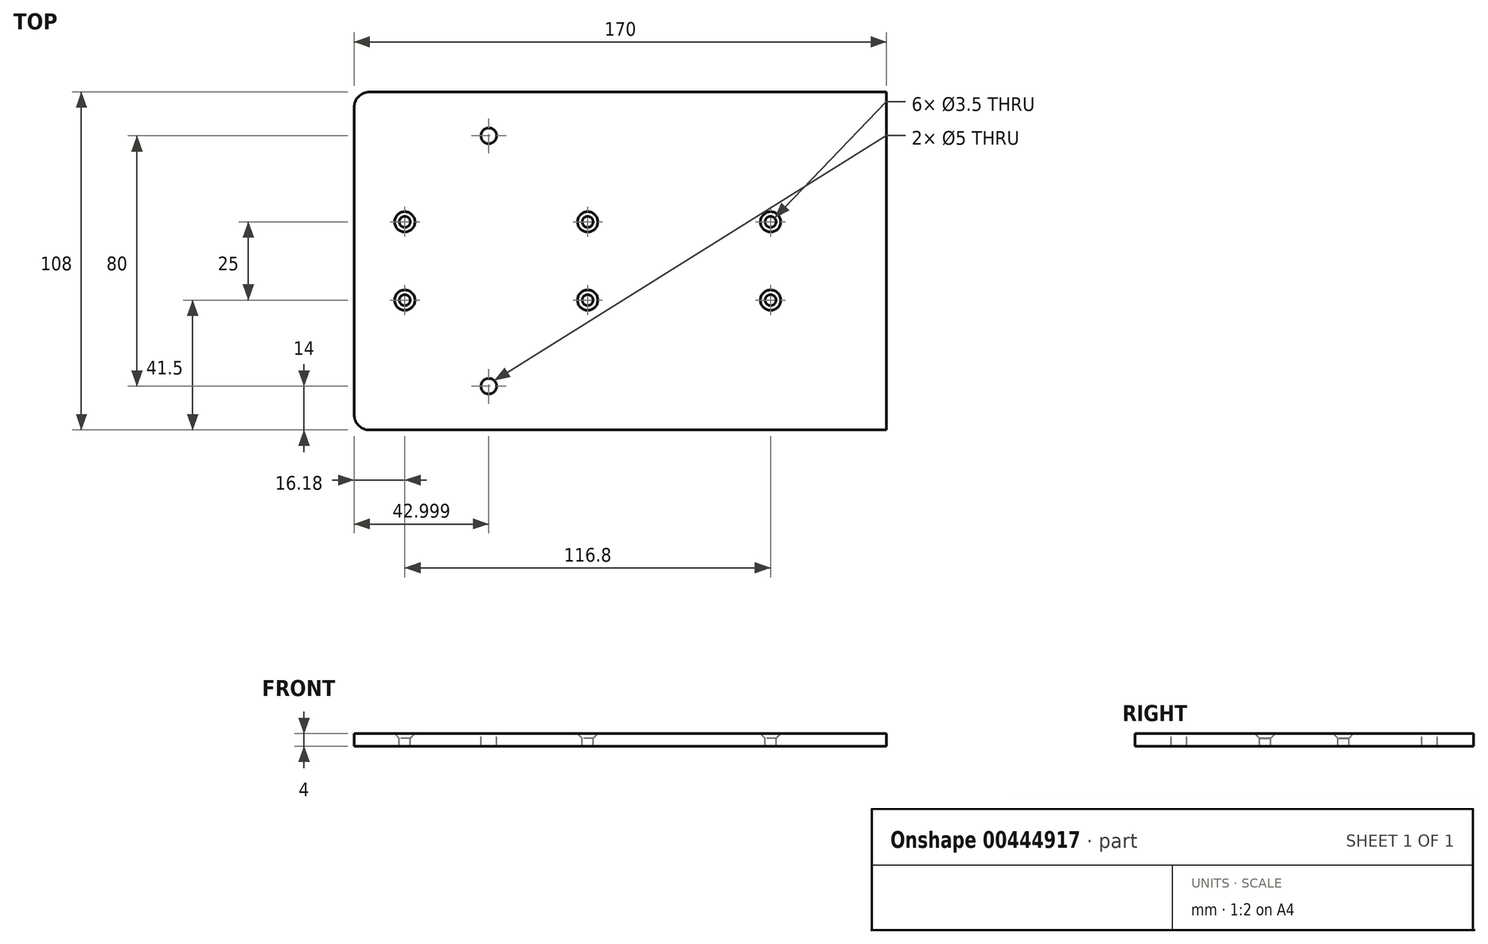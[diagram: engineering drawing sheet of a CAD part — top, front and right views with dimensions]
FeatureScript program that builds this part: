
annotation { "Feature Type Name" : "Feature", "Feature Type Description" : "" }
export const myFeature = defineFeature(function(context is Context, id is Id, definition is map)
    precondition{}
    {
        {
            var Q0;
            Q0=qCreatedBy(makeId("Top.planeOp"),FACE);
            var sketch = newSketch(context, id + "F0", { "sketchPlane" : qUnion([Q0])});
            skLineSegment(sketch, "E0.bottom", {"start": v(-74.58, 0) * mm, "end": v(95.42, 0) * mm});
            skLineSegment(sketch, "E0.top", {"start": v(-74.58, 54) * mm, "end": v(95.42, 54) * mm});
            skLineSegment(sketch, "E0.left", {"start": v(-74.58, 0) * mm, "end": v(-74.58, 54) * mm});
            skLineSegment(sketch, "E0.right", {"start": v(95.42, 0) * mm, "end": v(95.42, 54) * mm});
            skSolve(sketch);
        }
        {
            var Q0;
            Q0=makeQuery(id+"F0.imprint","IMPRINT",FACE,{"disambiguationData":[TD([[makeQuery(id+"F0.imprint","IMPRINT",EDGE,{"derivedFrom":sQuery(id+"F0.wireOp",EDGE,"E0.bottom")}),1.0]])]});
            extrude(context, id + "F1", {"entities" : qUnion([Q0]), "depth" : 4 * mm});
        }
        {
            var Q0;
            Q0=makeQuery(id+"F1.opExtrude","CAP_FACE",FACE,{"disambiguationData":[OSD([sQuery(id+"F0.wireOp",EDGE,"E0.bottom"),sQuery(id+"F0.wireOp",EDGE,"E0.top"),sQuery(id+"F0.wireOp",EDGE,"E0.left"),sQuery(id+"F0.wireOp",EDGE,"E0.right")])],"isStart":false});
            var sketch = newSketch(context, id + "F2", { "sketchPlane" : qUnion([Q0])});
            skPoint(sketch, "E1", {"position": v(-31.58, 40) * mm});
            skPoint(sketch, "E2", {"position": v(52.42, 40) * mm});
            skPoint(sketch, "E3", {"position": v(0, 12.5) * mm});
            skPoint(sketch, "E4", {"position": v(-58.4, 12.5) * mm});
            skPoint(sketch, "E5", {"position": v(58.4, 12.5) * mm});
            skSolve(sketch);
        }
        {
            var Q0;
            Q0=sQuery(id+"F2.wireOp",VERTEX,"E1");
            var Q1;
            Q1=makeQuery(id+"F1.opExtrude","SWEPT_BODY",BODY,{"disambiguationData":[OSD([sQuery(id+"F0.wireOp",EDGE,"E0.bottom"),sQuery(id+"F0.wireOp",EDGE,"E0.top"),sQuery(id+"F0.wireOp",EDGE,"E0.left"),sQuery(id+"F0.wireOp",EDGE,"E0.right")])]});
            hole(context, id + "F3", {"style" : HoleStyle.SIMPLE, "endStyle" : HoleEndStyle.THROUGH, "holeDiameter" : 5 * mm, "isTappedThrough" : true, "tappedDepth" : 12 * mm, "tapClearance" : 3, "startFromSketch" : true, "locations" : qUnion([Q0]), "scope" : qUnion([Q1])});
        }
        {
            var Q0;
            Q0=sQuery(id+"F2.wireOp",VERTEX,"E4");
            var Q1;
            Q1=sQuery(id+"F2.wireOp",VERTEX,"E3");
            var Q2;
            Q2=sQuery(id+"F2.wireOp",VERTEX,"E5");
            var Q3;
            Q3=makeQuery(id+"F1.opExtrude","SWEPT_BODY",BODY,{"disambiguationData":[OSD([sQuery(id+"F0.wireOp",EDGE,"E0.bottom"),sQuery(id+"F0.wireOp",EDGE,"E0.top"),sQuery(id+"F0.wireOp",EDGE,"E0.left"),sQuery(id+"F0.wireOp",EDGE,"E0.right")])]});
            hole(context, id + "F4", {"style" : HoleStyle.C_SINK, "endStyle" : HoleEndStyle.THROUGH, "holeDiameter" : 3.5 * mm, "cSinkDiameter" : 6.5 * mm, "cSinkAngle" : 90 * degree, "isTappedThrough" : true, "tappedDepth" : 12 * mm, "tapClearance" : 3, "startFromSketch" : true, "locations" : qUnion([Q0, Q1, Q2]), "scope" : qUnion([Q3])});
        }
        {
            var Q0;
            Q0=makeQuery(id+"F1.opExtrude","SWEPT_BODY",BODY,{"disambiguationData":[OSD([sQuery(id+"F0.wireOp",EDGE,"E0.bottom"),sQuery(id+"F0.wireOp",EDGE,"E0.top"),sQuery(id+"F0.wireOp",EDGE,"E0.left"),sQuery(id+"F0.wireOp",EDGE,"E0.right")])]});
            var Q1;
            Q1=makeQuery(id+"F1.opExtrude","SWEPT_FACE",FACE,{"disambiguationData":[OSD([sQuery(id+"F0.wireOp",EDGE,"E0.bottom")])]});
            mirror(context, id + "F5", {"operationType" : NewBodyOperationType.ADD, "entities" : qUnion([Q0]), "mirrorPlane" : qUnion([Q1])});
        }
        {
            var Q0;
            Q0=makeQuery(id+"F1.opExtrude","SWEPT_EDGE",EDGE,{"disambiguationData":[OSD([sQuery(id+"F0.wireOp",EDGE,"E0.top"),sQuery(id+"F0.wireOp",EDGE,"E0.left")])]});
            var Q1;
            Q1=makeQuery(id+"F5.opPattern","COPY",EDGE,{"derivedFrom":makeQuery(id+"F1.opExtrude","SWEPT_EDGE",EDGE,{"disambiguationData":[OSD([sQuery(id+"F0.wireOp",EDGE,"E0.top"),sQuery(id+"F0.wireOp",EDGE,"E0.left")])]}),"instanceName":"1"});
            fillet(context, id + "F6", {"entities" : qUnion([Q0, Q1]), "radius" : 5 * mm, "tangentPropagation" : true, "allowEdgeOverflow" : false});
        }
    });
